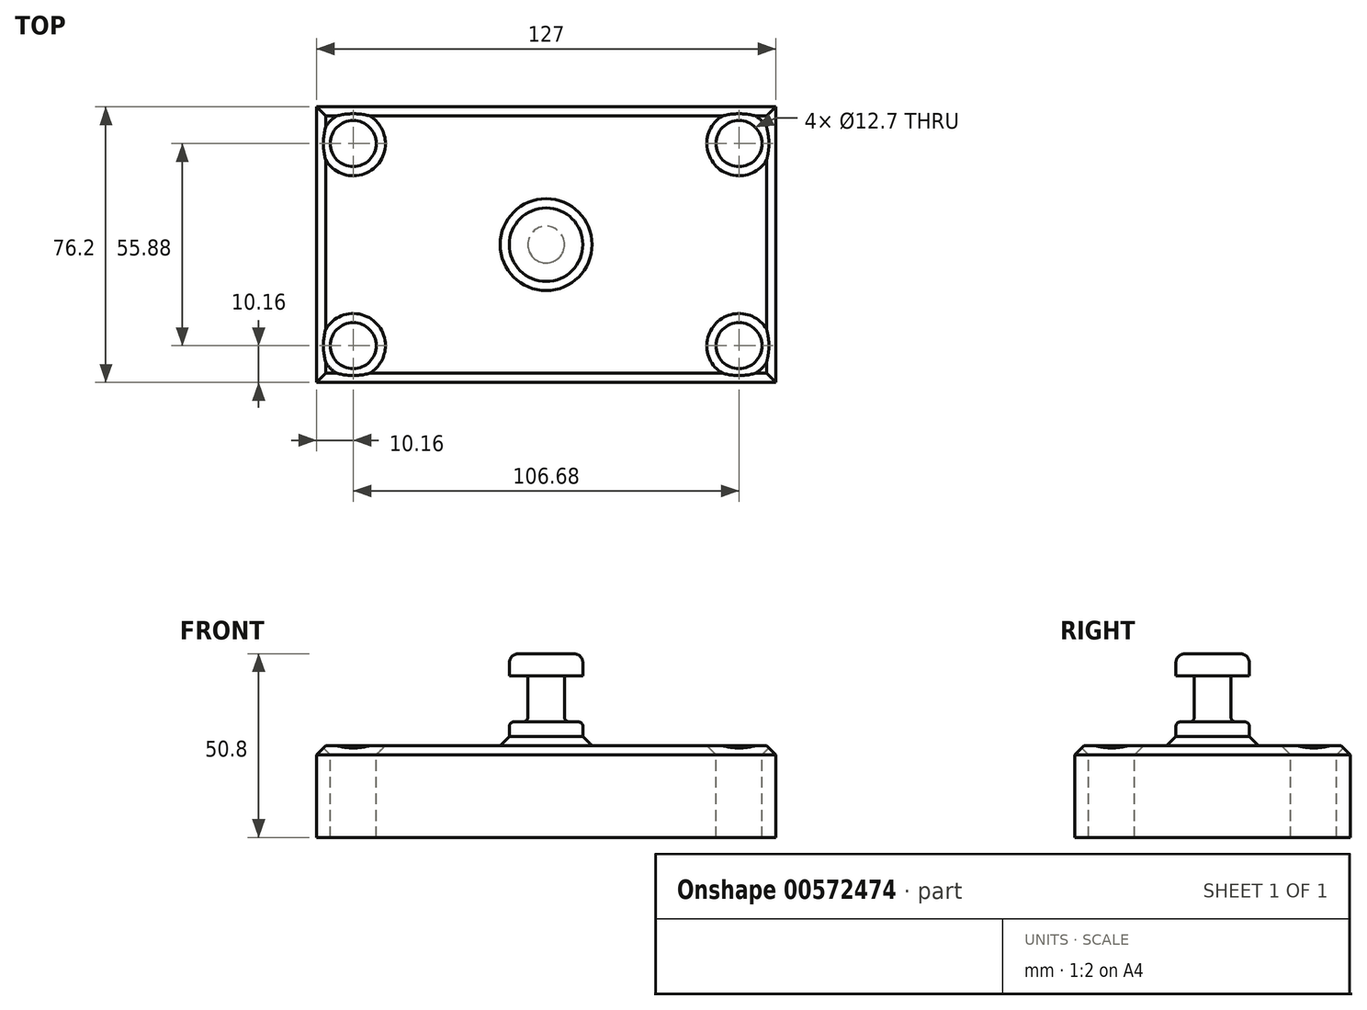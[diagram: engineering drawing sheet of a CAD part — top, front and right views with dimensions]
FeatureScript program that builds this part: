
annotation { "Feature Type Name" : "Feature", "Feature Type Description" : "" }
export const myFeature = defineFeature(function(context is Context, id is Id, definition is map)
    precondition{}
    {
        {
            var Q0;
            Q0=qCreatedBy(makeId("Top.planeOp"),FACE);
            var sketch = newSketch(context, id + "F0", { "sketchPlane" : qUnion([Q0])});
            skLineSegment(sketch, "E0.bottom", {"start": v(-63.5, 38.1) * mm, "end": v(63.5, 38.1) * mm});
            skLineSegment(sketch, "E0.top", {"start": v(-63.5, -38.1) * mm, "end": v(63.5, -38.1) * mm});
            skLineSegment(sketch, "E0.left", {"start": v(63.5, -38.1) * mm, "end": v(63.5, 38.1) * mm});
            skLineSegment(sketch, "E0.right", {"start": v(-63.5, -38.1) * mm, "end": v(-63.5, 38.1) * mm});
            skPoint(sketch, "E0.middle", {"position": v(0, 0) * mm});
            skSolve(sketch);
        }
        {
            var Q0;
            Q0=makeQuery(id+"F0.imprint","IMPRINT",FACE,{"disambiguationData":[TD([[makeQuery(id+"F0.imprint","IMPRINT",EDGE,{"derivedFrom":sQuery(id+"F0.wireOp",EDGE,"E0.bottom")}),-1.0]])]});
            extrude(context, id + "F1", {"entities" : qUnion([Q0]), "depth" : 25.4 * mm, "offsetDistance" : 25.4 * mm});
        }
        {
            var Q0;
            Q0=makeQuery(id+"F1.opExtrude","CAP_FACE",FACE,{"disambiguationData":[OSD([sQuery(id+"F0.wireOp",EDGE,"E0.bottom"),sQuery(id+"F0.wireOp",EDGE,"E0.top"),sQuery(id+"F0.wireOp",EDGE,"E0.left"),sQuery(id+"F0.wireOp",EDGE,"E0.right")])],"isStart":false});
            var sketch = newSketch(context, id + "F2", { "sketchPlane" : qUnion([Q0])});
            skCircle(sketch, "E1", {"center": v(53.34, 27.94) * mm, "radius": 6.35 * mm});
            skCircle(sketch, "E2", {"center": v(53.34, -27.94) * mm, "radius": 6.35 * mm});
            skCircle(sketch, "E3", {"center": v(-53.34, 27.94) * mm, "radius": 6.35 * mm});
            skCircle(sketch, "E4", {"center": v(-53.34, -27.94) * mm, "radius": 6.35 * mm});
            skSolve(sketch);
        }
        {
            var Q0;
            Q0 = qSketchRegion(id + "F2", true);
            extrude(context, id + "F3", {"entities" : qUnion([Q0]), "operationType" : NewBodyOperationType.REMOVE, "endBound" : BoundingType.THROUGH_ALL, "oppositeDirection" : true, "depth" : 25.4 * mm, "offsetDistance" : 25.4 * mm});
        }
        {
            var Q0;
            Q0=qCreatedBy(makeId("Front.planeOp"),FACE);
            var sketch = newSketch(context, id + "F4", { "sketchPlane" : qUnion([Q0])});
            skLineSegment(sketch, "E5.bottom", {"start": v(0, 50.8) * mm, "end": v(10.16, 50.8) * mm});
            skLineSegment(sketch, "E5.top", {"start": v(0, 25.4) * mm, "end": v(10.16, 25.4) * mm});
            skLineSegment(sketch, "E5.left", {"start": v(0, 50.8) * mm, "end": v(0, 25.4) * mm});
            skLineSegment(sketch, "E5.right", {"start": v(10.16, 50.8) * mm, "end": v(10.16, 25.4) * mm});
            skSolve(sketch);
        }
        {
            var Q0;
            Q0=makeQuery(id+"F4.imprint","IMPRINT",FACE,{"disambiguationData":[TD([[makeQuery(id+"F4.imprint","IMPRINT",EDGE,{"derivedFrom":sQuery(id+"F4.wireOp",EDGE,"E5.bottom")}),-1.0]])]});
            var Q1;
            Q1=sQuery(id+"F4.wireOp",EDGE,"E5.left");
            revolve(context, id + "F5", {"operationType" : NewBodyOperationType.ADD, "entities" : qUnion([Q0]), "axis" : qUnion([Q1]), "revolveType" : RevolveType.FULL});
        }
        {
            var Q0;
            Q0=qCreatedBy(makeId("Front.planeOp"),FACE);
            var sketch = newSketch(context, id + "F6", { "sketchPlane" : qUnion([Q0])});
            skLineSegment(sketch, "E6.bottom", {"start": v(20.32, 44.67) * mm, "end": v(5.08, 44.67) * mm});
            skLineSegment(sketch, "E6.top", {"start": v(20.32, 31.97) * mm, "end": v(5.08, 31.97) * mm});
            skLineSegment(sketch, "E6.left", {"start": v(20.32, 44.67) * mm, "end": v(20.32, 31.97) * mm});
            skLineSegment(sketch, "E6.right", {"start": v(5.08, 44.67) * mm, "end": v(5.08, 31.97) * mm});
            skSolve(sketch);
        }
        {
            var Q0;
            Q0 = qSketchRegion(id + "F6", true);
            var Q1;
            Q1=makeQuery(id+"F5.opRevolve","SWEPT_FACE",FACE,{"disambiguationData":[OSD([sQuery(id+"F4.wireOp",EDGE,"E5.right")])]});
            revolve(context, id + "F7", {"operationType" : NewBodyOperationType.REMOVE, "entities" : qUnion([Q0]), "axis" : qUnion([Q1]), "revolveType" : RevolveType.FULL, "oppositeDirection" : true});
        }
        {
            var Q0;
            Q0=makeQuery(id+"F5.opRevolve","SWEPT_EDGE",EDGE,{"disambiguationData":[OSD([sQuery(id+"F4.wireOp",EDGE,"E5.bottom"),sQuery(id+"F4.wireOp",EDGE,"E5.right")])]});
            fillet(context, id + "F8", {"entities" : qUnion([Q0]), "radius" : 2.54 * mm, "tangentPropagation" : true, "allowEdgeOverflow" : false});
        }
        {
            var Q0;
            Q0=makeQuery(id+"F7.boolean.opBoolean","COPY",FACE,{"derivedFrom":makeQuery(id+"F7.opRevolve","SWEPT_FACE",FACE,{"disambiguationData":[OSD([sQuery(id+"F6.wireOp",EDGE,"E6.top")])]})});
            var Q1;
            Q1=makeQuery(id+"F5.opRevolve","SWEPT_EDGE",EDGE,{"disambiguationData":[OSD([sQuery(id+"F4.wireOp",EDGE,"E5.top"),sQuery(id+"F4.wireOp",EDGE,"E5.right")])]});
            fillet(context, id + "F9", {"entities" : qUnion([Q0, Q1]), "radius" : 1.27 * mm, "tangentPropagation" : true, "allowEdgeOverflow" : false});
        }
        {
            var Q0;
            Q0=makeQuery(id+"F1.opExtrude","CAP_FACE",FACE,{"disambiguationData":[OSD([sQuery(id+"F0.wireOp",EDGE,"E0.bottom"),sQuery(id+"F0.wireOp",EDGE,"E0.top"),sQuery(id+"F0.wireOp",EDGE,"E0.left"),sQuery(id+"F0.wireOp",EDGE,"E0.right")])],"isStart":false});
            chamfer(context, id + "F10", {"entities" : qUnion([Q0]), "width" : 2.54 * mm, "tangentPropagation" : true});
        }
    });
